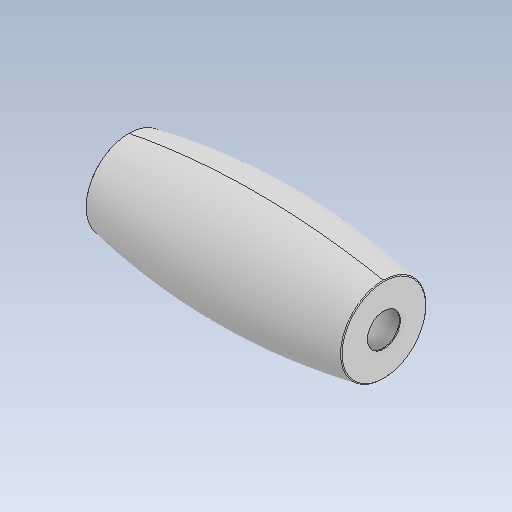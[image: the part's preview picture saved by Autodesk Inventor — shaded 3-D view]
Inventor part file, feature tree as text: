
AUTODESK INVENTOR PART (.ipt)
format: ipt  version: 2020.2 (Build 242310000, 310)  size: 155,136 bytes
history: native  units: in
note: dims shown in document units (in); Inventor stores cm internally (conversion verified against a paired STEP export)
features: fillet x1
ambient origin geometry x8: Origin, YZ Plane, XZ Plane, XY Plane, X Axis, Y Axis, Z Axis, Center Point
bodies: Solid1 (feature_tree)
feature tree (1):
  fillet  "Fillet1"  [1 undecoded]
note: 1 required parameter value undecoded (feature->parameter linkage not recoverable at this tier; creation-order binding heuristic only, values carry confidence <= 0.55)
